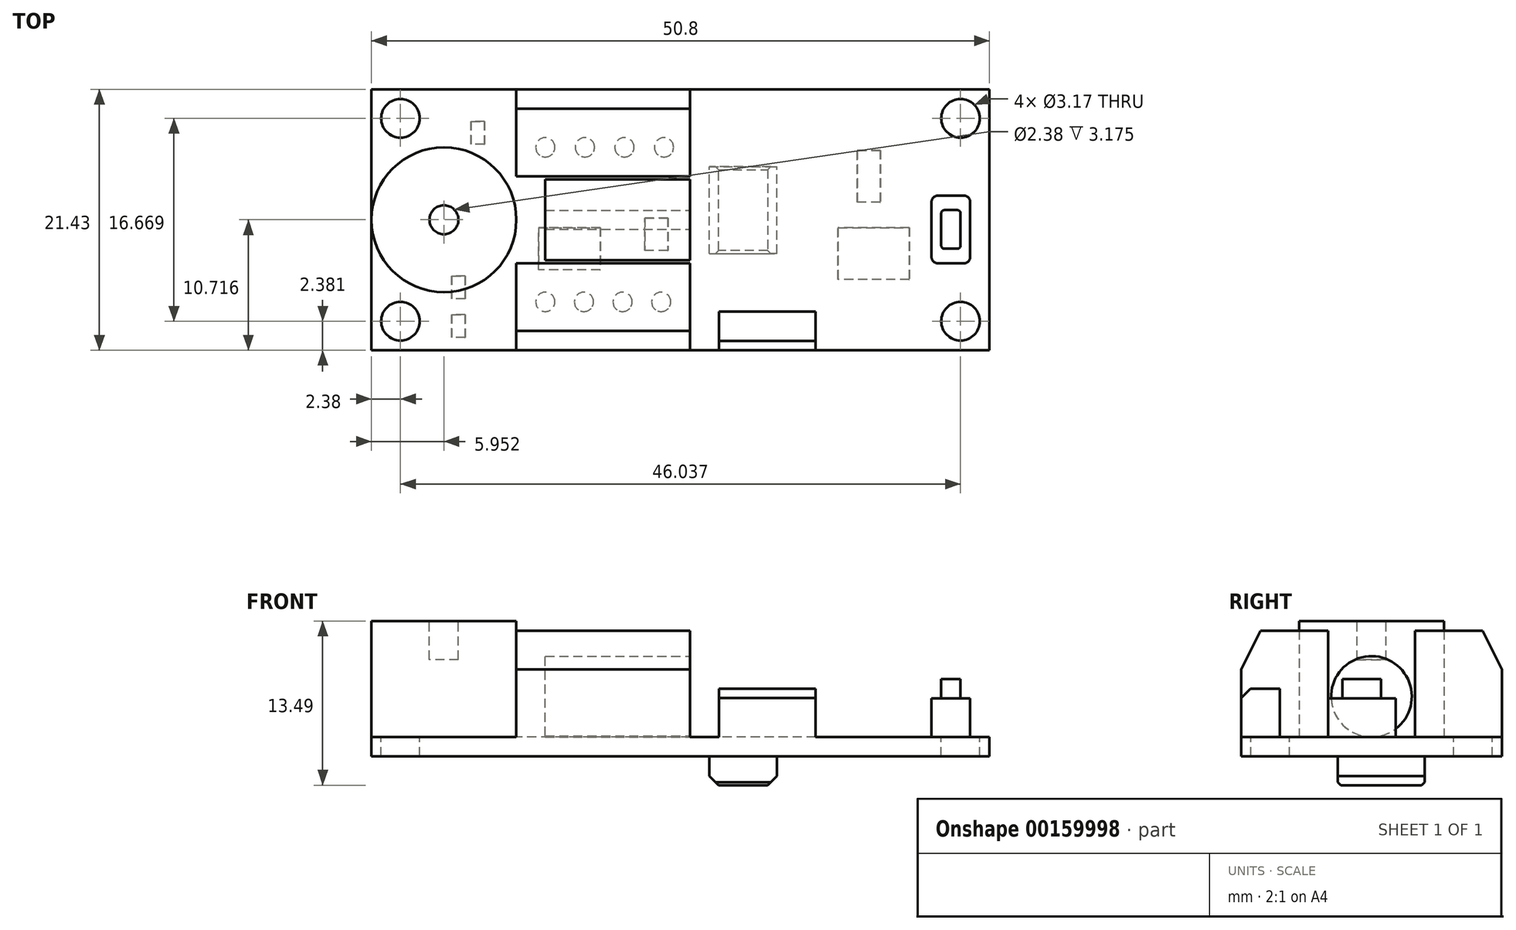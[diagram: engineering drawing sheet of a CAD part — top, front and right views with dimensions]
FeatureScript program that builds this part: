
annotation { "Feature Type Name" : "Feature", "Feature Type Description" : "" }
export const myFeature = defineFeature(function(context is Context, id is Id, definition is map)
    precondition{}
    {
        {
            var Q0;
            Q0=qCreatedBy(makeId("Top.planeOp"),FACE);
            var sketch = newSketch(context, id + "F0", { "sketchPlane" : qUnion([Q0])});
            skLineSegment(sketch, "E0.bottom", {"start": v(-22.64, -9.4) * mm, "end": v(28.16, -9.4) * mm});
            skLineSegment(sketch, "E0.top", {"start": v(-22.64, 12.03) * mm, "end": v(28.16, 12.03) * mm});
            skLineSegment(sketch, "E0.left", {"start": v(-22.64, -9.4) * mm, "end": v(-22.64, 12.03) * mm});
            skLineSegment(sketch, "E0.right", {"start": v(28.16, -9.4) * mm, "end": v(28.16, 12.03) * mm});
            skSolve(sketch);
        }
        {
            var Q0;
            Q0 = qSketchRegion(id + "F0", true);
            extrude(context, id + "F1", {"entities" : qUnion([Q0]), "depth" : 1.59 * mm});
        }
        {
            var Q0;
            Q0=makeQuery(id+"F1.opExtrude","CAP_FACE",FACE,{"disambiguationData":[OSD([sQuery(id+"F0.wireOp",EDGE,"E0.bottom"),sQuery(id+"F0.wireOp",EDGE,"E0.top"),sQuery(id+"F0.wireOp",EDGE,"E0.left"),sQuery(id+"F0.wireOp",EDGE,"E0.right")])],"isStart":false});
            var sketch = newSketch(context, id + "F2", { "sketchPlane" : qUnion([Q0])});
            skCircle(sketch, "E1", {"center": v(25.78, -7.02) * mm, "radius": 1.59 * mm});
            skCircle(sketch, "E2", {"center": v(25.78, 9.65) * mm, "radius": 1.59 * mm});
            skCircle(sketch, "E3", {"center": v(-20.26, 9.65) * mm, "radius": 1.59 * mm});
            skCircle(sketch, "E4", {"center": v(-20.26, -7.02) * mm, "radius": 1.59 * mm});
            skSolve(sketch);
        }
        {
            var Q0;
            Q0 = qSketchRegion(id + "F2", true);
            extrude(context, id + "F3", {"entities" : qUnion([Q0]), "operationType" : NewBodyOperationType.REMOVE, "oppositeDirection" : true, "depth" : 3.17 * mm});
        }
        {
            var Q0;
            Q0=makeQuery(id+"F1.opExtrude","CAP_FACE",FACE,{"disambiguationData":[OSD([sQuery(id+"F0.wireOp",EDGE,"E0.bottom"),sQuery(id+"F0.wireOp",EDGE,"E0.top"),sQuery(id+"F0.wireOp",EDGE,"E0.left"),sQuery(id+"F0.wireOp",EDGE,"E0.right")])],"isStart":true});
            var sketch = newSketch(context, id + "F4", { "sketchPlane" : qUnion([Q0])});
            skLineSegment(sketch, "E5.bottom", {"start": v(-9.94, -6.48) * mm, "end": v(2.76, -6.48) * mm});
            skLineSegment(sketch, "E5.top", {"start": v(-9.94, -8.06) * mm, "end": v(2.76, -8.06) * mm});
            skLineSegment(sketch, "E5.left", {"start": v(-9.94, -6.48) * mm, "end": v(-9.94, -8.06) * mm});
            skLineSegment(sketch, "E5.right", {"start": v(2.76, -6.48) * mm, "end": v(2.76, -8.06) * mm});
            skLineSegment(sketch, "E6.bottom", {"start": v(-9.94, 4.64) * mm, "end": v(2.76, 4.64) * mm});
            skLineSegment(sketch, "E6.top", {"start": v(-9.94, 6.22) * mm, "end": v(2.76, 6.22) * mm});
            skLineSegment(sketch, "E6.left", {"start": v(-9.94, 4.64) * mm, "end": v(-9.94, 6.22) * mm});
            skLineSegment(sketch, "E6.right", {"start": v(2.76, 4.64) * mm, "end": v(2.76, 6.22) * mm});
            skCircle(sketch, "E7", {"center": v(-8.35, 5.43) * mm, "radius": 0.8 * mm});
            skPoint(sketch, "E7.centerSnap0", {"position": v(-9.94, 5.43) * mm});
            skCircle(sketch, "E8.1.0.0", {"center": v(-5.18, 5.43) * mm, "radius": 0.8 * mm});
            skCircle(sketch, "E8.2.0.0", {"center": v(-2, 5.43) * mm, "radius": 0.8 * mm});
            skCircle(sketch, "E8.3.0.0", {"center": v(1.17, 5.43) * mm, "radius": 0.8 * mm});
            skLineSegment(sketch, "E8.direction1", {"start": v(-8.35, 5.43) * mm, "end": v(-5.18, 5.43) * mm, "construction": true});
            skCircle(sketch, "E9", {"center": v(-8.35, -7.27) * mm, "radius": 0.8 * mm});
            skPoint(sketch, "E9.centerSnap0", {"position": v(-9.94, -7.27) * mm});
            skCircle(sketch, "E10.1.0.0", {"center": v(-5.1, -7.27) * mm, "radius": 0.8 * mm});
            skCircle(sketch, "E10.2.0.0", {"center": v(-1.85, -7.27) * mm, "radius": 0.8 * mm});
            skCircle(sketch, "E10.3.0.0", {"center": v(1.4, -7.27) * mm, "radius": 0.8 * mm});
            skLineSegment(sketch, "E10.direction1", {"start": v(-8.35, -7.27) * mm, "end": v(-5.1, -7.27) * mm, "construction": true});
            skSolve(sketch);
        }
        {
            var Q0;
            {var subQ0=sQuery(id+"F4.wireOp",EDGE,"E8.1.0.0");var subQ1=makeQuery(id+"F4.imprint","INTERSECT",VERTEX,{"derivedFrom":[sQuery(id+"F4.wireOp",EDGE,"E6.bottom"),subQ0]});Q0=makeQuery(id+"F4.imprint","IMPRINT",FACE,{"disambiguationData":[TD([[makeQuery(id+"F4.imprint","IMPRINT",EDGE,{"disambiguationData":[TD([[subQ1,1.0]])],"derivedFrom":subQ0}),1.0]])]});}
            var Q1;
            {var subQ0=sQuery(id+"F4.wireOp",EDGE,"E8.2.0.0");var subQ1=makeQuery(id+"F4.imprint","INTERSECT",VERTEX,{"derivedFrom":[sQuery(id+"F4.wireOp",EDGE,"E6.bottom"),subQ0]});Q1=makeQuery(id+"F4.imprint","IMPRINT",FACE,{"disambiguationData":[TD([[makeQuery(id+"F4.imprint","IMPRINT",EDGE,{"disambiguationData":[TD([[subQ1,1.0]])],"derivedFrom":subQ0}),1.0]])]});}
            var Q2;
            {var subQ0=sQuery(id+"F4.wireOp",EDGE,"E8.3.0.0");var subQ1=makeQuery(id+"F4.imprint","INTERSECT",VERTEX,{"derivedFrom":[sQuery(id+"F4.wireOp",EDGE,"E6.bottom"),subQ0]});Q2=makeQuery(id+"F4.imprint","IMPRINT",FACE,{"disambiguationData":[TD([[makeQuery(id+"F4.imprint","IMPRINT",EDGE,{"disambiguationData":[TD([[subQ1,1.0]])],"derivedFrom":subQ0}),1.0]])]});}
            var Q3;
            {var subQ0=sQuery(id+"F4.wireOp",EDGE,"E9");var subQ1=makeQuery(id+"F4.imprint","INTERSECT",VERTEX,{"derivedFrom":[sQuery(id+"F4.wireOp",EDGE,"E5.bottom"),subQ0]});Q3=makeQuery(id+"F4.imprint","IMPRINT",FACE,{"disambiguationData":[TD([[makeQuery(id+"F4.imprint","IMPRINT",EDGE,{"disambiguationData":[TD([[subQ1,-1.0]])],"derivedFrom":subQ0}),1.0]])]});}
            var Q4;
            {var subQ0=sQuery(id+"F4.wireOp",EDGE,"E10.1.0.0");var subQ1=makeQuery(id+"F4.imprint","INTERSECT",VERTEX,{"derivedFrom":[sQuery(id+"F4.wireOp",EDGE,"E5.bottom"),subQ0]});Q4=makeQuery(id+"F4.imprint","IMPRINT",FACE,{"disambiguationData":[TD([[makeQuery(id+"F4.imprint","IMPRINT",EDGE,{"disambiguationData":[TD([[subQ1,-1.0]])],"derivedFrom":subQ0}),1.0]])]});}
            var Q5;
            {var subQ0=sQuery(id+"F4.wireOp",EDGE,"E10.2.0.0");var subQ1=makeQuery(id+"F4.imprint","INTERSECT",VERTEX,{"derivedFrom":[sQuery(id+"F4.wireOp",EDGE,"E5.bottom"),subQ0]});Q5=makeQuery(id+"F4.imprint","IMPRINT",FACE,{"disambiguationData":[TD([[makeQuery(id+"F4.imprint","IMPRINT",EDGE,{"disambiguationData":[TD([[subQ1,-1.0]])],"derivedFrom":subQ0}),1.0]])]});}
            var Q6;
            {var subQ0=sQuery(id+"F4.wireOp",EDGE,"E10.3.0.0");var subQ1=makeQuery(id+"F4.imprint","INTERSECT",VERTEX,{"derivedFrom":[sQuery(id+"F4.wireOp",EDGE,"E5.bottom"),subQ0]});Q6=makeQuery(id+"F4.imprint","IMPRINT",FACE,{"disambiguationData":[TD([[makeQuery(id+"F4.imprint","IMPRINT",EDGE,{"disambiguationData":[TD([[subQ1,-1.0]])],"derivedFrom":subQ0}),1.0]])]});}
            var Q7;
            {var subQ0=sQuery(id+"F4.wireOp",EDGE,"E7");var subQ1=makeQuery(id+"F4.imprint","INTERSECT",VERTEX,{"derivedFrom":[sQuery(id+"F4.wireOp",EDGE,"E6.bottom"),subQ0]});Q7=makeQuery(id+"F4.imprint","IMPRINT",FACE,{"disambiguationData":[TD([[makeQuery(id+"F4.imprint","IMPRINT",EDGE,{"disambiguationData":[TD([[subQ1,1.0]])],"derivedFrom":subQ0}),1.0]])]});}
            extrude(context, id + "F5", {"entities" : qUnion([Q0, Q1, Q2, Q3, Q4, Q5, Q6, Q7]), "operationType" : NewBodyOperationType.ADD, "depth" : 3 / 812.8 * mm});
        }
        {
            var Q0;
            Q0=makeQuery(id+"F1.opExtrude","CAP_FACE",FACE,{"disambiguationData":[OSD([sQuery(id+"F0.wireOp",EDGE,"E0.bottom"),sQuery(id+"F0.wireOp",EDGE,"E0.top"),sQuery(id+"F0.wireOp",EDGE,"E0.left"),sQuery(id+"F0.wireOp",EDGE,"E0.right")])],"isStart":true});
            var sketch = newSketch(context, id + "F6", { "sketchPlane" : qUnion([Q0])});
            skLineSegment(sketch, "E11.bottom", {"start": v(-16.3, 8.6) * mm, "end": v(-14.7, 8.6) * mm});
            skLineSegment(sketch, "E11.top", {"start": v(-16.3, 6.22) * mm, "end": v(-14.7, 6.22) * mm});
            skLineSegment(sketch, "E11.left", {"start": v(-16.3, 8.6) * mm, "end": v(-16.3, 6.22) * mm});
            skLineSegment(sketch, "E11.right", {"start": v(-14.7, 8.6) * mm, "end": v(-14.7, 6.22) * mm});
            skLineSegment(sketch, "E12.bottom", {"start": v(-16.3, 5.43) * mm, "end": v(-14.7, 5.43) * mm});
            skLineSegment(sketch, "E12.top", {"start": v(-16.3, 3.05) * mm, "end": v(-14.7, 3.05) * mm});
            skLineSegment(sketch, "E12.left", {"start": v(-16.3, 5.43) * mm, "end": v(-16.3, 3.05) * mm});
            skLineSegment(sketch, "E12.right", {"start": v(-14.7, 5.43) * mm, "end": v(-14.7, 3.05) * mm});
            skLineSegment(sketch, "E13.bottom", {"start": v(-14.7, -7.27) * mm, "end": v(-13.12, -7.27) * mm});
            skLineSegment(sketch, "E13.top", {"start": v(-14.7, -9.65) * mm, "end": v(-13.12, -9.65) * mm});
            skLineSegment(sketch, "E13.left", {"start": v(-14.7, -7.27) * mm, "end": v(-14.7, -9.65) * mm});
            skLineSegment(sketch, "E13.right", {"start": v(-13.12, -7.27) * mm, "end": v(-13.12, -9.65) * mm});
            skLineSegment(sketch, "E14.bottom", {"start": v(-9.15, 3.05) * mm, "end": v(-3.6, 3.05) * mm});
            skLineSegment(sketch, "E14.top", {"start": v(-9.15, -0.92) * mm, "end": v(-3.6, -0.92) * mm});
            skLineSegment(sketch, "E14.left", {"start": v(-9.15, 3.05) * mm, "end": v(-9.15, -0.92) * mm});
            skLineSegment(sketch, "E14.right", {"start": v(-3.6, 3.05) * mm, "end": v(-3.6, -0.92) * mm});
            skLineSegment(sketch, "E15.bottom", {"start": v(-0.42, 1.46) * mm, "end": v(1.97, 1.46) * mm});
            skLineSegment(sketch, "E15.top", {"start": v(-0.42, -1.71) * mm, "end": v(1.97, -1.71) * mm});
            skLineSegment(sketch, "E15.left", {"start": v(-0.42, 1.46) * mm, "end": v(-0.42, -1.71) * mm});
            skLineSegment(sketch, "E15.right", {"start": v(1.97, 1.46) * mm, "end": v(1.97, -1.71) * mm});
            skLineSegment(sketch, "E16.bottom", {"start": v(15.46, 3.84) * mm, "end": v(21.8, 3.84) * mm});
            skLineSegment(sketch, "E16.top", {"start": v(15.46, -0.92) * mm, "end": v(21.8, -0.92) * mm});
            skLineSegment(sketch, "E16.left", {"start": v(15.46, 3.84) * mm, "end": v(15.46, -0.92) * mm});
            skLineSegment(sketch, "E16.right", {"start": v(21.8, 3.84) * mm, "end": v(21.8, -0.92) * mm});
            skLineSegment(sketch, "E17.bottom", {"start": v(17.05, -2.5) * mm, "end": v(19.43, -2.5) * mm});
            skLineSegment(sketch, "E17.top", {"start": v(17.05, -7.27) * mm, "end": v(19.43, -7.27) * mm});
            skLineSegment(sketch, "E17.left", {"start": v(17.05, -2.5) * mm, "end": v(17.05, -7.27) * mm});
            skLineSegment(sketch, "E17.right", {"start": v(19.43, -2.5) * mm, "end": v(19.43, -7.27) * mm});
            skSolve(sketch);
        }
        {
            var Q0;
            Q0 = qSketchRegion(id + "F6", true);
            extrude(context, id + "F7", {"entities" : qUnion([Q0]), "operationType" : NewBodyOperationType.ADD, "depth" : 1 / 406.4 * mm});
        }
        {
            var Q0;
            Q0=makeQuery(id+"F7.opExtrude","CAP_FACE",FACE,{"disambiguationData":[OSD([sQuery(id+"F6.wireOp",EDGE,"E13.bottom"),sQuery(id+"F6.wireOp",EDGE,"E13.top"),sQuery(id+"F6.wireOp",EDGE,"E13.left"),sQuery(id+"F6.wireOp",EDGE,"E13.right")])],"isStart":false});
            var Q1;
            Q1=makeQuery(id+"F7.opExtrude","CAP_FACE",FACE,{"disambiguationData":[OSD([sQuery(id+"F6.wireOp",EDGE,"E12.bottom"),sQuery(id+"F6.wireOp",EDGE,"E12.top"),sQuery(id+"F6.wireOp",EDGE,"E12.left"),sQuery(id+"F6.wireOp",EDGE,"E12.right")])],"isStart":false});
            var Q2;
            Q2=makeQuery(id+"F7.opExtrude","CAP_FACE",FACE,{"disambiguationData":[OSD([sQuery(id+"F6.wireOp",EDGE,"E11.bottom"),sQuery(id+"F6.wireOp",EDGE,"E11.top"),sQuery(id+"F6.wireOp",EDGE,"E11.left"),sQuery(id+"F6.wireOp",EDGE,"E11.right")])],"isStart":false});
            var Q3;
            Q3=makeQuery(id+"F7.opExtrude","CAP_FACE",FACE,{"disambiguationData":[OSD([sQuery(id+"F6.wireOp",EDGE,"E14.bottom"),sQuery(id+"F6.wireOp",EDGE,"E14.top"),sQuery(id+"F6.wireOp",EDGE,"E14.left"),sQuery(id+"F6.wireOp",EDGE,"E14.right")])],"isStart":false});
            var Q4;
            Q4=makeQuery(id+"F7.opExtrude","CAP_FACE",FACE,{"disambiguationData":[OSD([sQuery(id+"F6.wireOp",EDGE,"E15.bottom"),sQuery(id+"F6.wireOp",EDGE,"E15.top"),sQuery(id+"F6.wireOp",EDGE,"E15.left"),sQuery(id+"F6.wireOp",EDGE,"E15.right")])],"isStart":false});
            var Q5;
            Q5=makeQuery(id+"F7.opExtrude","CAP_FACE",FACE,{"disambiguationData":[OSD([sQuery(id+"F6.wireOp",EDGE,"E16.bottom"),sQuery(id+"F6.wireOp",EDGE,"E16.top"),sQuery(id+"F6.wireOp",EDGE,"E16.left"),sQuery(id+"F6.wireOp",EDGE,"E16.right")])],"isStart":false});
            var Q6;
            Q6=makeQuery(id+"F7.opExtrude","CAP_FACE",FACE,{"disambiguationData":[OSD([sQuery(id+"F6.wireOp",EDGE,"E17.bottom"),sQuery(id+"F6.wireOp",EDGE,"E17.top"),sQuery(id+"F6.wireOp",EDGE,"E17.left"),sQuery(id+"F6.wireOp",EDGE,"E17.right")])],"isStart":false});
            chamfer(context, id + "F8", {"entities" : qUnion([Q0, Q1, Q2, Q3, Q4, Q5, Q6]), "width" : 0.25 * mm, "tangentPropagation" : true});
        }
        {
            var Q0;
            Q0=makeQuery(id+"F1.opExtrude","CAP_FACE",FACE,{"disambiguationData":[OSD([sQuery(id+"F0.wireOp",EDGE,"E0.bottom"),sQuery(id+"F0.wireOp",EDGE,"E0.top"),sQuery(id+"F0.wireOp",EDGE,"E0.left"),sQuery(id+"F0.wireOp",EDGE,"E0.right")])],"isStart":true});
            var sketch = newSketch(context, id + "F9", { "sketchPlane" : qUnion([Q0])});
            skLineSegment(sketch, "E18.bottom", {"start": v(5.14, 1.46) * mm, "end": v(10.7, 1.46) * mm});
            skLineSegment(sketch, "E18.top", {"start": v(5.14, -5.68) * mm, "end": v(10.7, -5.68) * mm});
            skLineSegment(sketch, "E18.left", {"start": v(5.14, 1.46) * mm, "end": v(5.14, -5.68) * mm});
            skLineSegment(sketch, "E18.right", {"start": v(10.7, 1.46) * mm, "end": v(10.7, -5.68) * mm});
            skSolve(sketch);
        }
        {
            var Q0;
            Q0 = qSketchRegion(id + "F9", true);
            extrude(context, id + "F10", {"entities" : qUnion([Q0]), "operationType" : NewBodyOperationType.ADD, "depth" : 2.38 * mm});
        }
        {
            var Q0;
            Q0=makeQuery(id+"F10.opExtrude","CAP_EDGE",EDGE,{"disambiguationData":[OSD([sQuery(id+"F9.wireOp",EDGE,"E18.right")])],"isStart":false});
            var Q1;
            Q1=makeQuery(id+"F10.opExtrude","CAP_EDGE",EDGE,{"disambiguationData":[OSD([sQuery(id+"F9.wireOp",EDGE,"E18.left")])],"isStart":false});
            chamfer(context, id + "F11", {"entities" : qUnion([Q0, Q1]), "width" : 0.76 * mm, "tangentPropagation" : true});
        }
        {
            var Q0;
            Q0=makeQuery(id+"F10.opExtrude","CAP_EDGE",EDGE,{"disambiguationData":[OSD([sQuery(id+"F9.wireOp",EDGE,"E18.bottom")])],"isStart":false});
            var Q1;
            Q1=makeQuery(id+"F10.opExtrude","CAP_EDGE",EDGE,{"disambiguationData":[OSD([sQuery(id+"F9.wireOp",EDGE,"E18.top")])],"isStart":false});
            chamfer(context, id + "F12", {"entities" : qUnion([Q0, Q1]), "width" : 0.25 * mm, "tangentPropagation" : true});
        }
        {
            var Q0;
            Q0=makeQuery(id+"F1.opExtrude","CAP_FACE",FACE,{"disambiguationData":[OSD([sQuery(id+"F0.wireOp",EDGE,"E0.bottom"),sQuery(id+"F0.wireOp",EDGE,"E0.top"),sQuery(id+"F0.wireOp",EDGE,"E0.left"),sQuery(id+"F0.wireOp",EDGE,"E0.right")])],"isStart":false});
            var sketch = newSketch(context, id + "F13", { "sketchPlane" : qUnion([Q0])});
            skCircle(sketch, "E19", {"center": v(-16.69, 1.32) * mm, "radius": 5.95 * mm});
            skSolve(sketch);
        }
        {
            var Q0;
            Q0 = qSketchRegion(id + "F13", true);
            extrude(context, id + "F14", {"entities" : qUnion([Q0]), "operationType" : NewBodyOperationType.ADD, "depth" : 9.52 * mm});
        }
        {
            var Q0;
            Q0=makeQuery(id+"F14.opExtrude","CAP_FACE",FACE,{"disambiguationData":[OSD([sQuery(id+"F13.wireOp",EDGE,"E19")])],"isStart":false});
            var sketch = newSketch(context, id + "F15", { "sketchPlane" : qUnion([Q0])});
            skCircle(sketch, "E20", {"center": v(-16.69, 1.32) * mm, "radius": 1.2 * mm});
            skSolve(sketch);
        }
        {
            var Q0;
            Q0 = qSketchRegion(id + "F15", true);
            extrude(context, id + "F16", {"entities" : qUnion([Q0]), "operationType" : NewBodyOperationType.REMOVE, "oppositeDirection" : true, "depth" : 3.17 * mm});
        }
        {
            var Q0;
            Q0=makeQuery(id+"F1.opExtrude","CAP_FACE",FACE,{"disambiguationData":[OSD([sQuery(id+"F0.wireOp",EDGE,"E0.bottom"),sQuery(id+"F0.wireOp",EDGE,"E0.top"),sQuery(id+"F0.wireOp",EDGE,"E0.left"),sQuery(id+"F0.wireOp",EDGE,"E0.right")])],"isStart":false});
            var sketch = newSketch(context, id + "F17", { "sketchPlane" : qUnion([Q0])});
            skLineSegment(sketch, "E21.bottom", {"start": v(3.55, 4.89) * mm, "end": v(-10.73, 4.89) * mm});
            skLineSegment(sketch, "E21.top", {"start": v(3.55, 12.03) * mm, "end": v(-10.73, 12.03) * mm});
            skLineSegment(sketch, "E21.left", {"start": v(3.55, 4.89) * mm, "end": v(3.55, 12.03) * mm});
            skLineSegment(sketch, "E21.right", {"start": v(-10.73, 4.89) * mm, "end": v(-10.73, 12.03) * mm});
            skLineSegment(sketch, "E22.bottom", {"start": v(3.55, -9.4) * mm, "end": v(-10.73, -9.4) * mm});
            skLineSegment(sketch, "E22.top", {"start": v(3.55, -2.26) * mm, "end": v(-10.73, -2.26) * mm});
            skLineSegment(sketch, "E22.left", {"start": v(3.55, -9.4) * mm, "end": v(3.55, -2.26) * mm});
            skLineSegment(sketch, "E22.right", {"start": v(-10.73, -9.4) * mm, "end": v(-10.73, -2.26) * mm});
            skSolve(sketch);
        }
        {
            var Q0;
            Q0 = qSketchRegion(id + "F17", true);
            extrude(context, id + "F18", {"entities" : qUnion([Q0]), "operationType" : NewBodyOperationType.ADD, "depth" : 8.73 * mm});
        }
        {
            var Q0;
            Q0=makeQuery(id+"F18.opExtrude","SWEPT_FACE",FACE,{"disambiguationData":[OSD([sQuery(id+"F17.wireOp",EDGE,"E22.left")])]});
            var sketch = newSketch(context, id + "F19", { "sketchPlane" : qUnion([Q0])});
            skLineSegment(sketch, "E23", {"start": v(-9.4, 7.14) * mm, "end": v(-7.81, 10.32) * mm});
            skLineSegment(sketch, "E24", {"start": v(-7.81, 10.32) * mm, "end": v(-6.85, 13.43) * mm});
            skLineSegment(sketch, "E25", {"start": v(-6.85, 13.43) * mm, "end": v(-12.62, 12.4) * mm});
            skLineSegment(sketch, "E26", {"start": v(-12.62, 12.4) * mm, "end": v(-9.4, 7.14) * mm});
            skLineSegment(sketch, "E27", {"start": v(10.44, 10.32) * mm, "end": v(12.03, 7.14) * mm});
            skLineSegment(sketch, "E28", {"start": v(12.03, 7.14) * mm, "end": v(15.65, 9.64) * mm});
            skLineSegment(sketch, "E29", {"start": v(15.65, 9.64) * mm, "end": v(16.47, 13.68) * mm});
            skLineSegment(sketch, "E30", {"start": v(16.47, 13.68) * mm, "end": v(11.74, 13.16) * mm});
            skLineSegment(sketch, "E31", {"start": v(11.74, 13.16) * mm, "end": v(10.44, 10.32) * mm});
            skSolve(sketch);
        }
        {
            var Q0;
            Q0 = qSketchRegion(id + "F19", true);
            extrude(context, id + "F20", {"entities" : qUnion([Q0]), "operationType" : NewBodyOperationType.REMOVE, "oppositeDirection" : true, "depth" : 15.24 * mm});
        }
        {
            var Q0;
            Q0=makeQuery(id+"F18.opExtrude","SWEPT_FACE",FACE,{"disambiguationData":[OSD([sQuery(id+"F17.wireOp",EDGE,"E22.left")])]});
            var sketch = newSketch(context, id + "F21", { "sketchPlane" : qUnion([Q0])});
            skCircle(sketch, "E32", {"center": v(1.32, 4.9) * mm, "radius": 3.32 * mm});
            skLineSegment(sketch, "E33.bottom", {"start": v(0.54, 1.68) * mm, "end": v(2.1, 1.68) * mm});
            skLineSegment(sketch, "E33.top", {"start": v(0.54, 1.53) * mm, "end": v(2.1, 1.53) * mm});
            skLineSegment(sketch, "E33.left", {"start": v(0.54, 1.68) * mm, "end": v(0.54, 1.53) * mm});
            skLineSegment(sketch, "E33.right", {"start": v(2.1, 1.68) * mm, "end": v(2.1, 1.53) * mm});
            skSolve(sketch);
        }
        {
            var Q0;
            Q0 = qSketchRegion(id + "F21", true);
            extrude(context, id + "F22", {"entities" : qUnion([Q0]), "operationType" : NewBodyOperationType.ADD, "oppositeDirection" : true, "depth" : 11.9 * mm});
        }
        {
            var Q0;
            Q0=makeQuery(id+"F1.opExtrude","CAP_FACE",FACE,{"disambiguationData":[OSD([sQuery(id+"F0.wireOp",EDGE,"E0.bottom"),sQuery(id+"F0.wireOp",EDGE,"E0.top"),sQuery(id+"F0.wireOp",EDGE,"E0.left"),sQuery(id+"F0.wireOp",EDGE,"E0.right")])],"isStart":false});
            var sketch = newSketch(context, id + "F23", { "sketchPlane" : qUnion([Q0])});
            skLineSegment(sketch, "E34.bottom", {"start": v(23.4, 3.3) * mm, "end": v(26.57, 3.3) * mm});
            skLineSegment(sketch, "E34.top", {"start": v(23.4, -2.26) * mm, "end": v(26.57, -2.26) * mm});
            skLineSegment(sketch, "E34.left", {"start": v(23.4, 3.3) * mm, "end": v(23.4, -2.26) * mm});
            skLineSegment(sketch, "E34.right", {"start": v(26.57, 3.3) * mm, "end": v(26.57, -2.26) * mm});
            skSolve(sketch);
        }
        {
            var Q0;
            Q0 = qSketchRegion(id + "F23", true);
            extrude(context, id + "F24", {"entities" : qUnion([Q0]), "operationType" : NewBodyOperationType.ADD, "depth" : 3.17 * mm});
        }
        {
            var Q0;
            Q0=makeQuery(id+"F24.opExtrude","CAP_FACE",FACE,{"disambiguationData":[OSD([sQuery(id+"F23.wireOp",EDGE,"E34.bottom"),sQuery(id+"F23.wireOp",EDGE,"E34.top"),sQuery(id+"F23.wireOp",EDGE,"E34.left"),sQuery(id+"F23.wireOp",EDGE,"E34.right")])],"isStart":false});
            var sketch = newSketch(context, id + "F25", { "sketchPlane" : qUnion([Q0])});
            skLineSegment(sketch, "E35.bottom", {"start": v(24.2, 2.1) * mm, "end": v(25.78, 2.1) * mm});
            skLineSegment(sketch, "E35.top", {"start": v(24.2, -1.07) * mm, "end": v(25.78, -1.07) * mm});
            skLineSegment(sketch, "E35.left", {"start": v(24.2, 2.1) * mm, "end": v(24.2, -1.07) * mm});
            skLineSegment(sketch, "E35.right", {"start": v(25.78, 2.1) * mm, "end": v(25.78, -1.07) * mm});
            skSolve(sketch);
        }
        {
            var Q0;
            Q0 = qSketchRegion(id + "F25", true);
            extrude(context, id + "F26", {"entities" : qUnion([Q0]), "operationType" : NewBodyOperationType.ADD, "depth" : 1.59 * mm});
        }
        {
            var Q0;
            Q0=makeQuery(id+"F26.opExtrude","SWEPT_EDGE",EDGE,{"disambiguationData":[OSD([sQuery(id+"F25.wireOp",EDGE,"E35.top"),sQuery(id+"F25.wireOp",EDGE,"E35.right")])]});
            var Q1;
            Q1=makeQuery(id+"F26.opExtrude","SWEPT_EDGE",EDGE,{"disambiguationData":[OSD([sQuery(id+"F25.wireOp",EDGE,"E35.top"),sQuery(id+"F25.wireOp",EDGE,"E35.left")])]});
            var Q2;
            Q2=makeQuery(id+"F26.opExtrude","SWEPT_EDGE",EDGE,{"disambiguationData":[OSD([sQuery(id+"F25.wireOp",EDGE,"E35.bottom"),sQuery(id+"F25.wireOp",EDGE,"E35.left")])]});
            var Q3;
            Q3=makeQuery(id+"F26.opExtrude","SWEPT_EDGE",EDGE,{"disambiguationData":[OSD([sQuery(id+"F25.wireOp",EDGE,"E35.bottom"),sQuery(id+"F25.wireOp",EDGE,"E35.right")])]});
            fillet(context, id + "F27", {"entities" : qUnion([Q0, Q1, Q2, Q3]), "radius" : 0.25 * mm, "tangentPropagation" : true, "allowEdgeOverflow" : false});
        }
        {
            var Q0;
            Q0=makeQuery(id+"F24.opExtrude","SWEPT_EDGE",EDGE,{"disambiguationData":[OSD([sQuery(id+"F23.wireOp",EDGE,"E34.bottom"),sQuery(id+"F23.wireOp",EDGE,"E34.right")])]});
            var Q1;
            Q1=makeQuery(id+"F24.opExtrude","SWEPT_EDGE",EDGE,{"disambiguationData":[OSD([sQuery(id+"F23.wireOp",EDGE,"E34.bottom"),sQuery(id+"F23.wireOp",EDGE,"E34.left")])]});
            var Q2;
            Q2=makeQuery(id+"F24.opExtrude","SWEPT_EDGE",EDGE,{"disambiguationData":[OSD([sQuery(id+"F23.wireOp",EDGE,"E34.top"),sQuery(id+"F23.wireOp",EDGE,"E34.right")])]});
            var Q3;
            Q3=makeQuery(id+"F24.opExtrude","SWEPT_EDGE",EDGE,{"disambiguationData":[OSD([sQuery(id+"F23.wireOp",EDGE,"E34.top"),sQuery(id+"F23.wireOp",EDGE,"E34.left")])]});
            fillet(context, id + "F28", {"entities" : qUnion([Q0, Q1, Q2, Q3]), "radius" : 0.5 * mm, "tangentPropagation" : true, "allowEdgeOverflow" : false});
        }
        {
            var Q0;
            Q0=makeQuery(id+"F1.opExtrude","CAP_FACE",FACE,{"disambiguationData":[OSD([sQuery(id+"F0.wireOp",EDGE,"E0.bottom"),sQuery(id+"F0.wireOp",EDGE,"E0.top"),sQuery(id+"F0.wireOp",EDGE,"E0.left"),sQuery(id+"F0.wireOp",EDGE,"E0.right")])],"isStart":false});
            var sketch = newSketch(context, id + "F29", { "sketchPlane" : qUnion([Q0])});
            skLineSegment(sketch, "E36.bottom", {"start": v(13.87, -6.22) * mm, "end": v(5.93, -6.22) * mm});
            skLineSegment(sketch, "E36.top", {"start": v(13.87, -9.4) * mm, "end": v(5.93, -9.4) * mm});
            skLineSegment(sketch, "E36.left", {"start": v(13.87, -6.22) * mm, "end": v(13.87, -9.4) * mm});
            skLineSegment(sketch, "E36.right", {"start": v(5.93, -6.22) * mm, "end": v(5.93, -9.4) * mm});
            skSolve(sketch);
        }
        {
            var Q0;
            Q0 = qSketchRegion(id + "F29", true);
            extrude(context, id + "F30", {"entities" : qUnion([Q0]), "operationType" : NewBodyOperationType.ADD, "depth" : 3.97 * mm});
        }
        {
            var Q0;
            Q0=makeQuery(id+"F30.opExtrude","CAP_EDGE",EDGE,{"disambiguationData":[OSD([sQuery(id+"F29.wireOp",EDGE,"E36.top")])],"isStart":false});
            chamfer(context, id + "F31", {"entities" : qUnion([Q0]), "width" : 0.76 * mm, "tangentPropagation" : true});
        }
    });
